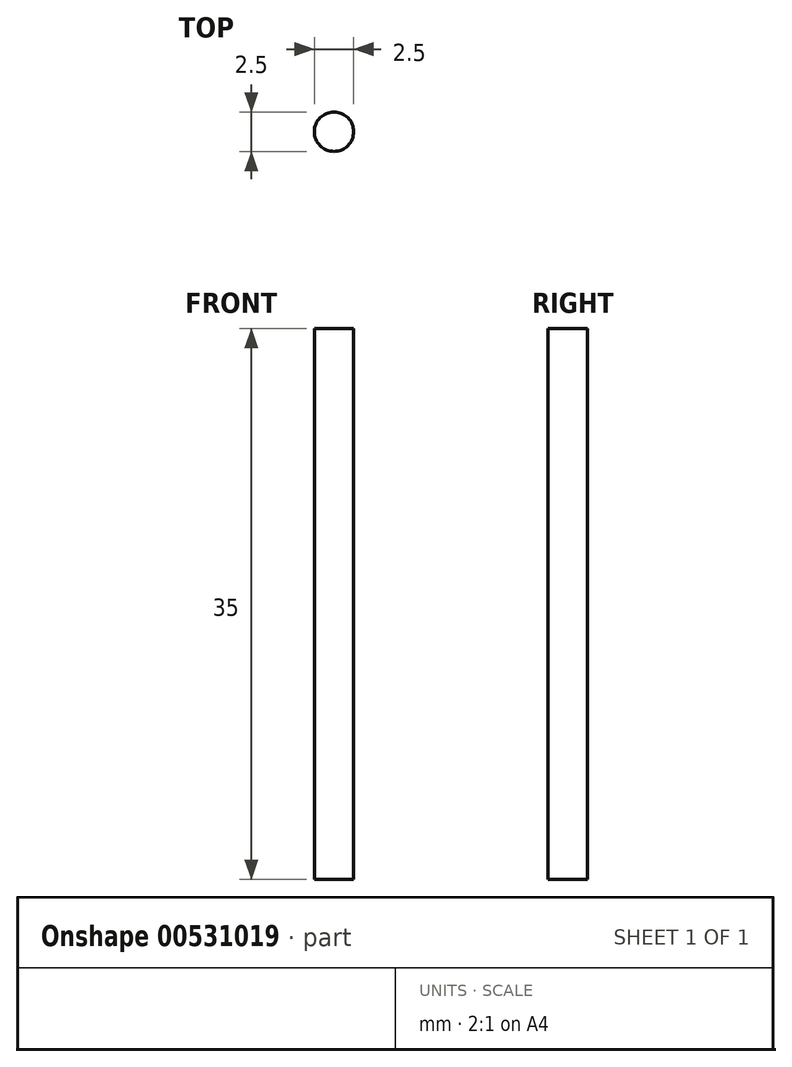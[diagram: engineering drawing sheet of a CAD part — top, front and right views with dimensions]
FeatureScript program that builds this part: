
annotation { "Feature Type Name" : "Feature", "Feature Type Description" : "" }
export const myFeature = defineFeature(function(context is Context, id is Id, definition is map)
    precondition{}
    {
        {
            var Q0;
            Q0=qCreatedBy(makeId("Top.planeOp"),FACE);
            var sketch = newSketch(context, id + "F0", { "sketchPlane" : qUnion([Q0])});
            skCircle(sketch, "E0", {"center": v(0, 0) * mm, "radius": 1.25 * mm});
            skSolve(sketch);
        }
        {
            var Q0;
            Q0 = qSketchRegion(id + "F0", true);
            extrude(context, id + "F1", {"entities" : qUnion([Q0]), "depth" : 35 * mm, "offsetDistance" : 25 * mm});
        }
    });
